# Revit family: QF_BPRO_RWR 160_572934
name_source: partatom
category: Sonderausstattung
revit_build: Autodesk Revit 2018 (Build: 20190510_1515(x64)
units: mm (PartAtom-declared; Revit-internal decimal feet)

## family parameters
Arbeitsebenenbasiert = Nein
Beim Laden mit Abzugskörper schneiden = Nein
Bemaßung runder Anschluss = Durchmesser verwenden
Gemeinsam genutzt = Nein
Immer vertikal = Ja
Raumberechnungspunkt = Ja
Teiletyp = Normal

## types (1)
- RWR 160
    Abstand Einlagen = 73 mm
    Anzahl Schienen = 18
    Artikel Nummer = 572934
    Beschreibung = Regalwagen aus rostfreiem Edelstahl
Auflagenabstand: 18 Paar 73 mm
Kapazität: 18 GN 1/1 oder  36 GN 1/2
Tragfähigkeit: 200 kg
Wandabweiser aus Kunststoff (Polyamid) an allen vier Ecken
    Beschreibung durch Hersteller analog Leistungsverzeichniskurztext = Abmessungen

Länge:			460 mm
Breite:			613 mm
Höhe:			1645 mm

Lichtes Maß:
Abstand der Auflagenschienen:  73 mm


Ausführung

Der Regalwagen besteht aus CNS 18/10, Werkstoff-Nr. 1.4301. Zwischen stabilem Vierkant-rohr mit 25 x 25 mm (gebogen ohne Einzug) befinden sich eingeschweißte U-Profil-Führungsschienen. Diese sind mit einer Kippsicherung sowie einer beidseitigen Durchschubsicherung für GN 1/1, 2/3, 1/2 ,1/3, 2/8 versehen.
Ein eingeschweißtes Vierkantrohr 20 x 10 mm auf mittlerer Höhe des Regalwagens, jeweils an Vorder- und Rückseite höhenversetzt angebracht, verstärkt zusätzlich die Stabilität.

Der Regalwagen ist fahrbar mittels rostfreien Kunststoffrollen gemäß DIN 18867, Teil 8
(4 Lenkrollen, davon 2 mit Feststeller, Rollendurchmesser 125 mm). Wandabweiser aus Kunststoff (Polyamid) an allen vier Ecken schützen vor Beschädigung.

Zubehör/ Optionen

•	Staubschutzhaube aus durchsichtigem PE (Best.Nr. 568 771)
•	Isolierhaube aus PE, beidseitig aluminiert (Best.Nr. 568 774)
•	Wagendach aus CNS
•	CNS-Verkleidung, 2- oder 3-seitig
•	Transportsicherungsbügel, beidseitig
•	Schiebegriff stirnseitig


 
Technische Daten

Werkstoff:		Chromnickelstahl 18/10,
		                        Polyamid (PA)
Materialstärke VK-Rohr:	1,5 mm
Materialstärke
Auflageschienen:		1,2 mm
Gewicht:		                        19 kg
Tragfähigkeit je Wagen:	200 kg
Anzahl Auflagenpaare:	18
Kapazität:		18 x GN 1/1 oder
		36 x GN 1/2


Besonderheit

•	U-Profil-Führungsschienen mit Kipp- und beidseitiger Durchschubsicherung


Fabrikat

Hersteller:	B.PRO
Typ:                                      RWR 160
Best.Nr.		572 934
    Beschreibung durch Hersteller analog Leistungsverzeichnislangtext = Abmessungen

Länge:			460 mm
Breite:			613 mm
Höhe:			1645 mm

Lichtes Maß:
Abstand der Auflagenschienen:  73 mm


Ausführung

Der Regalwagen besteht aus CNS 18/10, Werkstoff-Nr. 1.4301. Zwischen stabilem Vierkant-rohr mit 25 x 25 mm (gebogen ohne Einzug) befinden sich eingeschweißte U-Profil-Führungsschienen. Diese sind mit einer Kippsicherung sowie einer beidseitigen Durchschubsicherung für GN 1/1, 2/3, 1/2 ,1/3, 2/8 versehen.
Ein eingeschweißtes Vierkantrohr 20 x 10 mm auf mittlerer Höhe des Regalwagens, jeweils an Vorder- und Rückseite höhenversetzt angebracht, verstärkt zusätzlich die Stabilität.

Der Regalwagen ist fahrbar mittels rostfreien Kunststoffrollen gemäß DIN 18867, Teil 8
(4 Lenkrollen, davon 2 mit Feststeller, Rollendurchmesser 125 mm). Wandabweiser aus Kunststoff (Polyamid) an allen vier Ecken schützen vor Beschädigung.

Zubehör/ Optionen

•	Staubschutzhaube aus durchsichtigem PE (Best.Nr. 568 771)
•	Isolierhaube aus PE, beidseitig aluminiert (Best.Nr. 568 774)
•	Wagendach aus CNS
•	CNS-Verkleidung, 2- oder 3-seitig
•	Transportsicherungsbügel, beidseitig
•	Schiebegriff stirnseitig


 
Technische Daten

Werkstoff:		Chromnickelstahl 18/10,
		                        Polyamid (PA)
Materialstärke VK-Rohr:	1,5 mm
Materialstärke
Auflageschienen:		1,2 mm
Gewicht:		                        19 kg
Tragfähigkeit je Wagen:	200 kg
Anzahl Auflagenpaare:	18
Kapazität:		18 x GN 1/1 oder
		36 x GN 1/2


Besonderheit

•	U-Profil-Führungsschienen mit Kipp- und beidseitiger Durchschubsicherung


Fabrikat

Hersteller:	B.PRO
Typ:                                      RWR 160
Best.Nr.		572 934
    Gerätegewicht Netto = 19.00 kg
    Großküchengerätezuordnung = Ja
    Hersteller = B.PRO GmbH
    Höhe = 1645 mm  [stored 5.39698 ft]
    Internetadresse Gerätehersteller = https://www.bpro-solutions.com
    Internetadresse für Ersatzteilliste = https://www.bpro-solutions.com
    Kosten = 565.9 $
    Länge Gerätebreite = 460 mm  [stored 1.50919 ft]
    Länge Korpus = 385 mm  [stored 1.26312 ft]
    Material = QF_Metal-Stainless-Steel_general
    Material_Stoßschutz = QF_Rubber-Black-Matt
    Modell = RWR 160
    Sockelhöhe = 174 mm  [stored 0.570866 ft]
    Tiefe = 613 mm
    Tiefe Korpus = 538 mm  [stored 1.76509 ft]
    Typenkommentare = Regalwagen, 1-teilig
    URL = https://www.bpro-solutions.com
    Versatz Einlage unten = 65 mm
    Zubehör = Nein

note: [stored X ft] marks values corroborated as IEEE doubles in the binary element streams (Revit-internal decimal feet)
